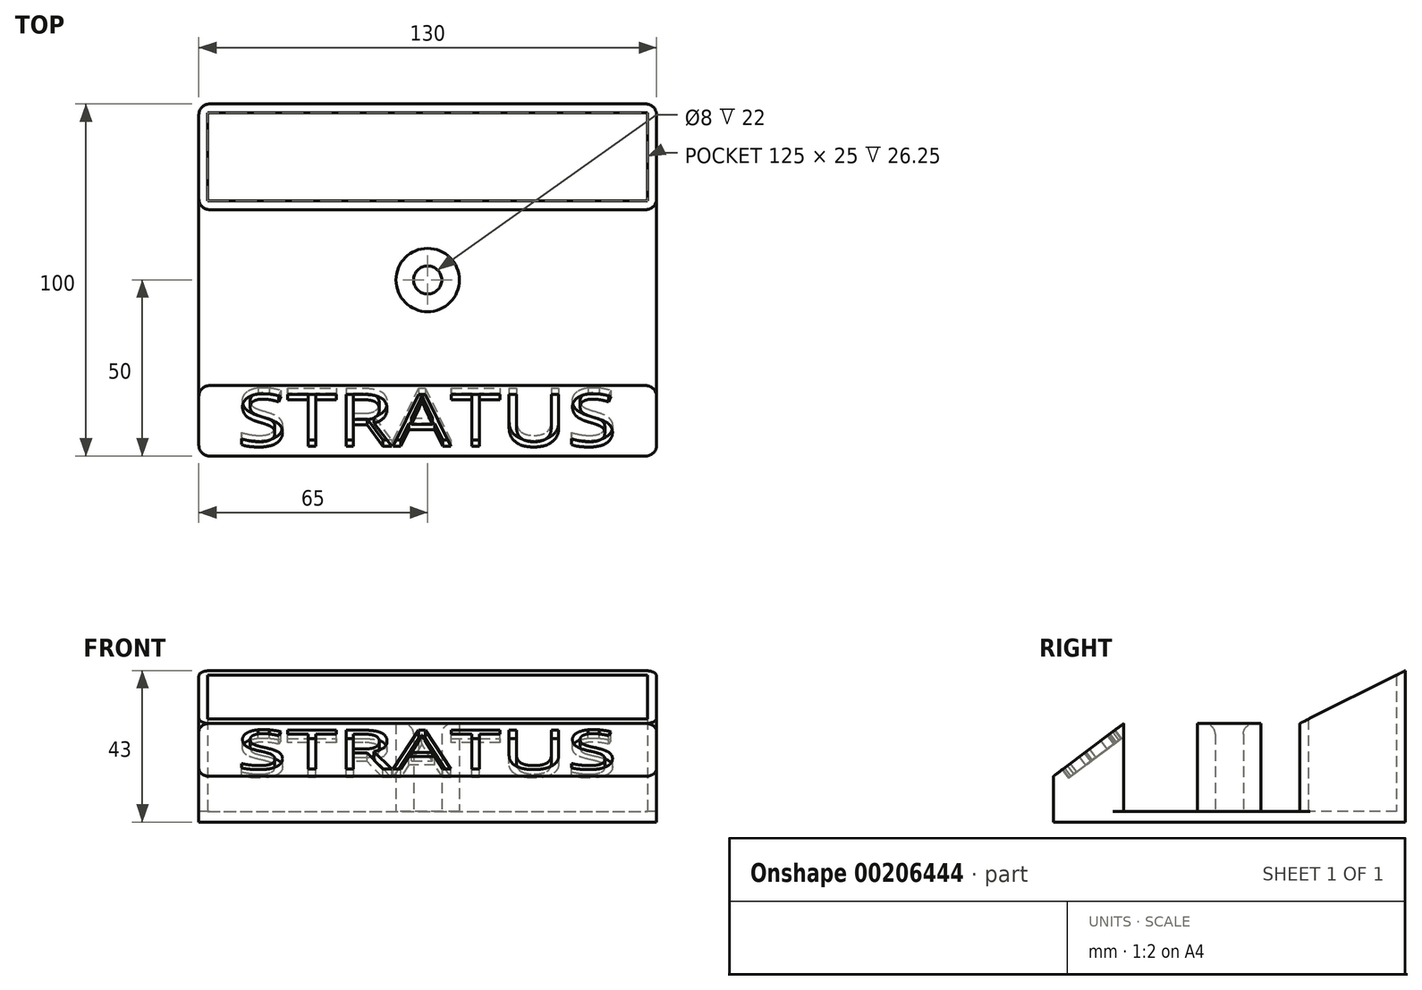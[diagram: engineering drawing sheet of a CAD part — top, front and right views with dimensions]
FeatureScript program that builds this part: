
annotation { "Feature Type Name" : "Feature", "Feature Type Description" : "" }
export const myFeature = defineFeature(function(context is Context, id is Id, definition is map)
    precondition{}
    {
        {
            var Q0;
            Q0=qCreatedBy(makeId("Top.planeOp"),FACE);
            var sketch = newSketch(context, id + "F0", { "sketchPlane" : qUnion([Q0])});
            skLineSegment(sketch, "E0.bottom", {"start": v(-65, 100) * mm, "end": v(65, 100) * mm});
            skLineSegment(sketch, "E0.top", {"start": v(-65, 0) * mm, "end": v(65, 0) * mm});
            skLineSegment(sketch, "E0.left", {"start": v(65, 100) * mm, "end": v(65, 0) * mm});
            skLineSegment(sketch, "E0.right", {"start": v(-65, 100) * mm, "end": v(-65, 0) * mm});
            skSolve(sketch);
        }
        {
            var Q0;
            Q0=makeQuery(id+"F0.imprint","IMPRINT",FACE,{"disambiguationData":[TD([[makeQuery(id+"F0.imprint","IMPRINT",EDGE,{"derivedFrom":sQuery(id+"F0.wireOp",EDGE,"E0.bottom")}),-1.0]])]});
            extrude(context, id + "F1", {"entities" : qUnion([Q0]), "depth" : 3 * mm});
        }
        {
            var Q0;
            Q0=makeQuery(id+"F1.opExtrude","CAP_FACE",FACE,{"disambiguationData":[OSD([sQuery(id+"F0.wireOp",EDGE,"E0.bottom"),sQuery(id+"F0.wireOp",EDGE,"E0.top"),sQuery(id+"F0.wireOp",EDGE,"E0.left"),sQuery(id+"F0.wireOp",EDGE,"E0.right")])],"isStart":false});
            var sketch = newSketch(context, id + "F2", { "sketchPlane" : qUnion([Q0])});
            skLineSegment(sketch, "E1", {"start": v(0, 0) * mm, "end": v(0, 100) * mm, "construction": true});
            skCircle(sketch, "E2", {"center": v(0, 50) * mm, "radius": 9 * mm});
            skCircle(sketch, "E3", {"center": v(0, 50) * mm, "radius": 4 * mm});
            skLineSegment(sketch, "E4.bottom", {"start": v(-65, 0) * mm, "end": v(65, 0) * mm});
            skLineSegment(sketch, "E4.top", {"start": v(-65, 20) * mm, "end": v(65, 20) * mm});
            skLineSegment(sketch, "E4.left", {"start": v(-65, 0) * mm, "end": v(-65, 20) * mm});
            skLineSegment(sketch, "E4.right", {"start": v(65, 0) * mm, "end": v(65, 20) * mm});
            skLineSegment(sketch, "E5.bottom", {"start": v(-65, 100) * mm, "end": v(65, 100) * mm});
            skLineSegment(sketch, "E5.top", {"start": v(-65, 70) * mm, "end": v(65, 70) * mm});
            skLineSegment(sketch, "E5.left", {"start": v(-65, 100) * mm, "end": v(-65, 70) * mm});
            skLineSegment(sketch, "E5.right", {"start": v(65, 100) * mm, "end": v(65, 70) * mm});
            skLineSegment(sketch, "E6.0", {"start": v(62.5, 97.5) * mm, "end": v(62.5, 72.5) * mm});
            skLineSegment(sketch, "E6.1", {"start": v(-62.5, 97.5) * mm, "end": v(62.5, 97.5) * mm});
            skLineSegment(sketch, "E6.2", {"start": v(-62.5, 97.5) * mm, "end": v(-62.5, 72.5) * mm});
            skLineSegment(sketch, "E6.3", {"start": v(-62.5, 72.5) * mm, "end": v(62.5, 72.5) * mm});
            skSolve(sketch);
        }
        {
            var Q0;
            Q0=makeQuery(id+"F2.imprint","IMPRINT",FACE,{"disambiguationData":[TD([[makeQuery(id+"F2.imprint","IMPRINT",EDGE,{"derivedFrom":sQuery(id+"F2.wireOp",EDGE,"E5.bottom")}),-1.0]])]});
            extrude(context, id + "F3", {"entities" : qUnion([Q0]), "operationType" : NewBodyOperationType.ADD, "depth" : 40 * mm});
        }
        {
            var Q0;
            Q0=makeQuery(id+"F2.imprint","IMPRINT",FACE,{"disambiguationData":[TD([[makeQuery(id+"F2.imprint","IMPRINT",EDGE,{"derivedFrom":sQuery(id+"F2.wireOp",EDGE,"E2")}),1.0]])]});
            var Q1;
            Q1=makeQuery(id+"F2.imprint","IMPRINT",FACE,{"disambiguationData":[TD([[makeQuery(id+"F2.imprint","IMPRINT",EDGE,{"derivedFrom":sQuery(id+"F2.wireOp",EDGE,"E4.bottom")}),1.0]])]});
            extrude(context, id + "F4", {"entities" : qUnion([Q0, Q1]), "operationType" : NewBodyOperationType.ADD, "depth" : 25 * mm});
        }
        {
            var Q0;
            Q0=makeQuery(id+"F4.opExtrude","CAP_EDGE",EDGE,{"disambiguationData":[OSD([sQuery(id+"F2.wireOp",EDGE,"E4.bottom")])],"isStart":false});
            chamfer(context, id + "F5", {"entities" : qUnion([Q0]), "chamferType" : ChamferType.TWO_OFFSETS, "width1" : 20 * mm, "oppositeDirection" : false, "width2" : 15 * mm, "tangentPropagation" : true});
        }
        {
            var Q0;
            Q0=makeQuery(id+"F3.opExtrude","CAP_EDGE",EDGE,{"disambiguationData":[OSD([sQuery(id+"F2.wireOp",EDGE,"E5.top")])],"isStart":false});
            chamfer(context, id + "F6", {"entities" : qUnion([Q0]), "chamferType" : ChamferType.TWO_OFFSETS, "width1" : 30 * mm, "oppositeDirection" : false, "width2" : 15 * mm, "tangentPropagation" : true});
        }
        {
            var Q0;
            Q0=makeQuery(id+"F3.boolean.opBoolean","MERGE",EDGE,{"derivedFrom":[makeQuery(id+"F1.opExtrude","SWEPT_EDGE",EDGE,{"disambiguationData":[OSD([sQuery(id+"F0.wireOp",EDGE,"E0.bottom"),sQuery(id+"F0.wireOp",EDGE,"E0.right")])]}),makeQuery(id+"F3.opExtrude","SWEPT_EDGE",EDGE,{"disambiguationData":[OSD([sQuery(id+"F2.wireOp",EDGE,"E5.bottom"),sQuery(id+"F2.wireOp",EDGE,"E5.left")])]})]});
            var Q1;
            Q1=makeQuery(id+"F3.opExtrude","SWEPT_EDGE",EDGE,{"disambiguationData":[OSD([sQuery(id+"F0.wireOp",EDGE,"E0.right"),sQuery(id+"F2.wireOp",EDGE,"E5.top"),sQuery(id+"F2.wireOp",EDGE,"E5.left")])]});
            var Q2;
            Q2=makeQuery(id+"F3.opExtrude","SWEPT_EDGE",EDGE,{"disambiguationData":[OSD([sQuery(id+"F0.wireOp",EDGE,"E0.left"),sQuery(id+"F2.wireOp",EDGE,"E5.top"),sQuery(id+"F2.wireOp",EDGE,"E5.right")])]});
            var Q3;
            Q3=makeQuery(id+"F4.boolean.opBoolean","MERGE",EDGE,{"derivedFrom":[makeQuery(id+"F1.opExtrude","SWEPT_EDGE",EDGE,{"disambiguationData":[OSD([sQuery(id+"F0.wireOp",EDGE,"E0.top"),sQuery(id+"F0.wireOp",EDGE,"E0.right")])]}),makeQuery(id+"F4.opExtrude","SWEPT_EDGE",EDGE,{"disambiguationData":[OSD([sQuery(id+"F2.wireOp",EDGE,"E4.bottom"),sQuery(id+"F2.wireOp",EDGE,"E4.left")])]})]});
            var Q4;
            Q4=makeQuery(id+"F3.boolean.opBoolean","MERGE",EDGE,{"derivedFrom":[makeQuery(id+"F1.opExtrude","SWEPT_EDGE",EDGE,{"disambiguationData":[OSD([sQuery(id+"F0.wireOp",EDGE,"E0.bottom"),sQuery(id+"F0.wireOp",EDGE,"E0.left")])]}),makeQuery(id+"F3.opExtrude","SWEPT_EDGE",EDGE,{"disambiguationData":[OSD([sQuery(id+"F2.wireOp",EDGE,"E5.bottom"),sQuery(id+"F2.wireOp",EDGE,"E5.right")])]})]});
            var Q5;
            Q5=makeQuery(id+"F4.boolean.opBoolean","MERGE",EDGE,{"derivedFrom":[makeQuery(id+"F1.opExtrude","SWEPT_EDGE",EDGE,{"disambiguationData":[OSD([sQuery(id+"F0.wireOp",EDGE,"E0.top"),sQuery(id+"F0.wireOp",EDGE,"E0.left")])]}),makeQuery(id+"F4.opExtrude","SWEPT_EDGE",EDGE,{"disambiguationData":[OSD([sQuery(id+"F2.wireOp",EDGE,"E4.bottom"),sQuery(id+"F2.wireOp",EDGE,"E4.right")])]})]});
            var Q6;
            Q6=makeQuery(id+"F4.opExtrude","SWEPT_EDGE",EDGE,{"disambiguationData":[OSD([sQuery(id+"F0.wireOp",EDGE,"E0.left"),sQuery(id+"F2.wireOp",EDGE,"E4.top"),sQuery(id+"F2.wireOp",EDGE,"E4.right")])]});
            var Q7;
            Q7=makeQuery(id+"F4.opExtrude","SWEPT_EDGE",EDGE,{"disambiguationData":[OSD([sQuery(id+"F0.wireOp",EDGE,"E0.right"),sQuery(id+"F2.wireOp",EDGE,"E4.top"),sQuery(id+"F2.wireOp",EDGE,"E4.left")])]});
            var Q8;
            Q8=makeQuery(id+"F4.opExtrude","CAP_EDGE",EDGE,{"disambiguationData":[OSD([sQuery(id+"F2.wireOp",EDGE,"E3")])],"isStart":false});
            fillet(context, id + "F7", {"entities" : qUnion([Q0, Q1, Q2, Q3, Q4, Q5, Q6, Q7, Q8]), "radius" : 3 * mm, "tangentPropagation" : true, "allowEdgeOverflow" : false});
        }
        {
            var Q0;
            Q0=makeQuery(id+"F5.opChamfer","BLEND_FACE",FACE,{"disambiguationData":[OSD([sQuery(id+"F2.wireOp",EDGE,"E4.bottom")])]});
            var sketch = newSketch(context, id + "F8", { "sketchPlane" : qUnion([Q0])});
            skLineSegment(sketch, "E7.0", {"start": v(62, 10.8) * mm, "end": v(-62, 10.8) * mm});
            skLineSegment(sketch, "E8.0", {"start": v(-62, 29.8) * mm, "end": v(62, 29.8) * mm});
            skText(sketch, "E9", { "text": "STRATUS", "fontName": "OpenSans-Regular.ttf"});
            skLineSegment(sketch, "E10", {"start": v(-62, 10.8) * mm, "end": v(-62, 47.82) * mm});
            skLineSegment(sketch, "E11", {"start": v(62, 10.8) * mm, "end": v(62, 49.07) * mm});
            skPoint(sketch, "E11.endSnap0", {"position": v(62, 15.3) * mm});
            const initialGuessF8  = {"E9": [-0.05416, 0.01123, 1, 0, 0.01857]};
            skSetInitialGuess(sketch, initialGuessF8);
            skSolve(sketch);
        }
        {
            var Q0;
            Q0=makeQuery(id+"F8.imprint","IMPRINT",FACE,{"disambiguationData":[TD([[makeQuery(id+"F8.imprint","IMPRINT",EDGE,{"derivedFrom":sQuery(id+"F8.wireOp",EDGE,"E9.sketch_text.stroke-0")}),-1.0]])]});
            var Q1;
            Q1=makeQuery(id+"F8.imprint","IMPRINT",FACE,{"disambiguationData":[TD([[makeQuery(id+"F8.imprint","IMPRINT",EDGE,{"derivedFrom":sQuery(id+"F8.wireOp",EDGE,"E9.sketch_text.stroke-13")}),-1.0]])]});
            var Q2;
            Q2=makeQuery(id+"F8.imprint","IMPRINT",FACE,{"disambiguationData":[TD([[makeQuery(id+"F8.imprint","IMPRINT",EDGE,{"derivedFrom":sQuery(id+"F8.wireOp",EDGE,"E9.sketch_text.stroke-19")}),-1.0]])]});
            var Q3;
            Q3=makeQuery(id+"F8.imprint","IMPRINT",FACE,{"disambiguationData":[TD([[makeQuery(id+"F8.imprint","IMPRINT",EDGE,{"derivedFrom":sQuery(id+"F8.wireOp",EDGE,"E9.sketch_text.stroke-27")}),-1.0]])]});
            var Q4;
            Q4=makeQuery(id+"F8.imprint","IMPRINT",FACE,{"disambiguationData":[TD([[makeQuery(id+"F8.imprint","IMPRINT",EDGE,{"derivedFrom":sQuery(id+"F8.wireOp",EDGE,"E9.sketch_text.stroke-43")}),-1.0]])]});
            var Q5;
            Q5=makeQuery(id+"F8.imprint","IMPRINT",FACE,{"disambiguationData":[TD([[makeQuery(id+"F8.imprint","IMPRINT",EDGE,{"derivedFrom":sQuery(id+"F8.wireOp",EDGE,"E9.sketch_text.stroke-58")}),-1.0]])]});
            var Q6;
            Q6=makeQuery(id+"F8.imprint","IMPRINT",FACE,{"disambiguationData":[TD([[makeQuery(id+"F8.imprint","IMPRINT",EDGE,{"derivedFrom":sQuery(id+"F8.wireOp",EDGE,"E9.sketch_text.stroke-72")}),-1.0]])]});
            var Q7;
            Q7=makeQuery(id+"F8.imprint","IMPRINT",FACE,{"disambiguationData":[TD([[makeQuery(id+"F8.imprint","IMPRINT",EDGE,{"derivedFrom":sQuery(id+"F8.wireOp",EDGE,"E9.sketch_text.stroke-90")}),-1.0]])]});
            var Q8;
            Q8=makeQuery(id+"F8.imprint","IMPRINT",FACE,{"disambiguationData":[TD([[makeQuery(id+"F8.imprint","IMPRINT",EDGE,{"derivedFrom":sQuery(id+"F8.wireOp",EDGE,"E9.sketch_text.stroke-104")}),-1.0]])]});
            var Q9;
            Q9=makeQuery(id+"F8.imprint","IMPRINT",FACE,{"disambiguationData":[TD([[makeQuery(id+"F8.imprint","IMPRINT",EDGE,{"derivedFrom":sQuery(id+"F8.wireOp",EDGE,"E9.sketch_text.stroke-110")}),-1.0]])]});
            var Q10;
            Q10=makeQuery(id+"F8.imprint","IMPRINT",FACE,{"disambiguationData":[TD([[makeQuery(id+"F8.imprint","IMPRINT",EDGE,{"derivedFrom":sQuery(id+"F8.wireOp",EDGE,"E9.sketch_text.stroke-64")}),-1.0]])]});
            extrude(context, id + "F9", {"entities" : qUnion([Q0, Q1, Q2, Q3, Q4, Q5, Q6, Q7, Q8, Q9, Q10]), "operationType" : NewBodyOperationType.REMOVE, "oppositeDirection" : true, "depth" : 3 * mm});
        }
    });
